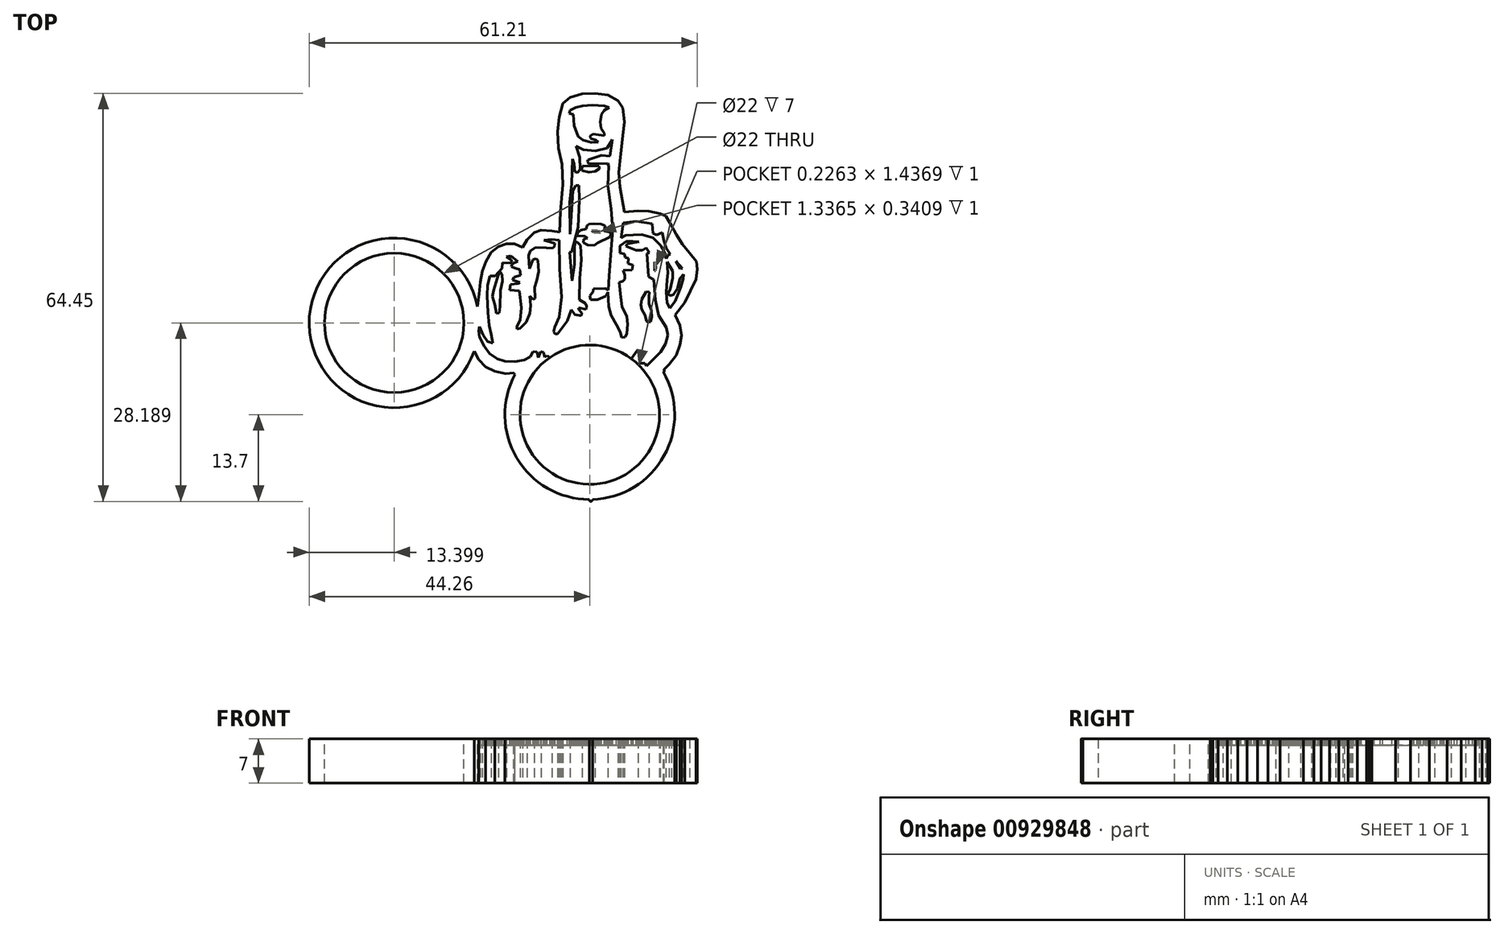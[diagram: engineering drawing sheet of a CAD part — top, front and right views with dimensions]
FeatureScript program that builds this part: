
annotation { "Feature Type Name" : "Feature", "Feature Type Description" : "" }
export const myFeature = defineFeature(function(context is Context, id is Id, definition is map)
    precondition{}
    {
        {
            var Q0;
            Q0=qCreatedBy(makeId("Top.planeOp"),FACE);
            var sketch = newSketch(context, id + "F0", { "sketchPlane" : qUnion([Q0])});
            skCircle(sketch, "E0", {"center": v(0, 0) * mm, "radius": 11 * mm});
            skCircle(sketch, "E1", {"center": v(0, 0) * mm, "radius": 13.4 * mm});
            skCircle(sketch, "E2", {"center": v(0, 0) * mm, "radius": 50.8 * mm, "construction": true});
            skLineSegment(sketch, "E3", {"start": v(0, 0) * mm, "end": v(-44, 25.4) * mm, "construction": true});
            skLineSegment(sketch, "E4", {"start": v(0, 0) * mm, "end": v(44, 25.4) * mm, "construction": true});
            skLineSegment(sketch, "E5", {"start": v(0, 0) * mm, "end": v(0, -50.8) * mm, "construction": true});
            skSolve(sketch);
        }
        {
            var Q0;
            Q0=qCreatedBy(makeId("Top.planeOp"),FACE);
            var sketch = newSketch(context, id + "F1", { "sketchPlane" : qUnion([Q0])});
            skCircle(sketch, "E6.0", {"center": v(0, 0) * mm, "radius": 13.4 * mm});
            skLineSegment(sketch, "E7", {"start": v(-11.66, 6.6) * mm, "end": v(-13.26, 6.5) * mm});
            skLineSegment(sketch, "E8", {"start": v(-13.26, 6.5) * mm, "end": v(-14.97, 6.82) * mm});
            skLineSegment(sketch, "E9", {"start": v(-14.97, 6.82) * mm, "end": v(-16.42, 7.53) * mm});
            skLineSegment(sketch, "E10", {"start": v(-16.42, 7.53) * mm, "end": v(-17.5, 8.7) * mm});
            skLineSegment(sketch, "E11", {"start": v(-17.5, 8.7) * mm, "end": v(-18.45, 10.38) * mm});
            skLineSegment(sketch, "E12", {"start": v(-18.45, 10.38) * mm, "end": v(-18.8, 12.26) * mm});
            skLineSegment(sketch, "E13", {"start": v(-18.8, 12.26) * mm, "end": v(-18.53, 13.84) * mm});
            skLineSegment(sketch, "E14", {"start": v(-18.53, 13.84) * mm, "end": v(-18.08, 14.9) * mm});
            skLineSegment(sketch, "E15", {"start": v(-18.08, 14.9) * mm, "end": v(-17.8, 16.19) * mm});
            skLineSegment(sketch, "E16", {"start": v(-17.8, 16.19) * mm, "end": v(-17.65, 17.63) * mm});
            skLineSegment(sketch, "E17", {"start": v(-17.65, 17.63) * mm, "end": v(-17.47, 19.02) * mm});
            skLineSegment(sketch, "E18", {"start": v(-17.47, 19.02) * mm, "end": v(-17.24, 20.92) * mm});
            skLineSegment(sketch, "E19", {"start": v(-17.24, 20.92) * mm, "end": v(-16.93, 22.67) * mm});
            skLineSegment(sketch, "E20", {"start": v(-16.93, 22.67) * mm, "end": v(-16.4, 24.2) * mm});
            skLineSegment(sketch, "E21", {"start": v(-16.4, 24.2) * mm, "end": v(-15.57, 25.63) * mm});
            skLineSegment(sketch, "E22", {"start": v(-15.57, 25.63) * mm, "end": v(-14.42, 26.52) * mm});
            skLineSegment(sketch, "E23", {"start": v(-14.42, 26.52) * mm, "end": v(-13.13, 26.99) * mm});
            skLineSegment(sketch, "E24", {"start": v(-13.13, 26.99) * mm, "end": v(-11.88, 26.99) * mm});
            skLineSegment(sketch, "E25", {"start": v(-11.88, 26.99) * mm, "end": v(-10.57, 26.44) * mm});
            skLineSegment(sketch, "E26", {"start": v(-10.57, 26.44) * mm, "end": v(-9.87, 27.6) * mm});
            skLineSegment(sketch, "E27", {"start": v(-9.87, 27.6) * mm, "end": v(-8.74, 28.74) * mm});
            skLineSegment(sketch, "E28", {"start": v(-8.74, 28.74) * mm, "end": v(-7.67, 29.15) * mm});
            skLineSegment(sketch, "E29", {"start": v(-7.67, 29.15) * mm, "end": v(-5.97, 29.04) * mm});
            skLineSegment(sketch, "E30", {"start": v(-5.97, 29.04) * mm, "end": v(-4.76, 28.84) * mm});
            skLineSegment(sketch, "E31", {"start": v(-4.76, 28.84) * mm, "end": v(-4.65, 32.06) * mm});
            skLineSegment(sketch, "E32", {"start": v(-4.65, 32.06) * mm, "end": v(-4.28, 36.3) * mm});
            skLineSegment(sketch, "E33", {"start": v(-4.28, 36.3) * mm, "end": v(-4.38, 39.56) * mm});
            skLineSegment(sketch, "E34", {"start": v(-4.38, 39.56) * mm, "end": v(-4.93, 42.06) * mm});
            skLineSegment(sketch, "E35", {"start": v(-4.93, 42.06) * mm, "end": v(-5.07, 44.68) * mm});
            skLineSegment(sketch, "E36", {"start": v(-5.07, 44.68) * mm, "end": v(-4.82, 46.97) * mm});
            skLineSegment(sketch, "E37", {"start": v(-4.82, 46.97) * mm, "end": v(-4.26, 49.12) * mm});
            skLineSegment(sketch, "E38", {"start": v(-4.26, 49.12) * mm, "end": v(-3.1, 50.06) * mm});
            skLineSegment(sketch, "E39", {"start": v(-3.1, 50.06) * mm, "end": v(-1.2, 50.67) * mm});
            skLineSegment(sketch, "E40", {"start": v(-1.2, 50.67) * mm, "end": v(0.84, 50.75) * mm});
            skLineSegment(sketch, "E41", {"start": v(0.84, 50.75) * mm, "end": v(2.84, 50.46) * mm});
            skLineSegment(sketch, "E42", {"start": v(2.84, 50.46) * mm, "end": v(4.45, 49.59) * mm});
            skLineSegment(sketch, "E43", {"start": v(4.45, 49.59) * mm, "end": v(5.24, 48.46) * mm});
            skLineSegment(sketch, "E44", {"start": v(5.24, 48.46) * mm, "end": v(5.47, 46.25) * mm});
            skLineSegment(sketch, "E45", {"start": v(5.47, 46.25) * mm, "end": v(5.24, 44.04) * mm});
            skLineSegment(sketch, "E46", {"start": v(5.24, 44.04) * mm, "end": v(4.88, 41.23) * mm});
            skLineSegment(sketch, "E47", {"start": v(4.88, 41.23) * mm, "end": v(4.6, 38.26) * mm});
            skLineSegment(sketch, "E48", {"start": v(4.6, 38.26) * mm, "end": v(4.78, 35.9) * mm});
            skLineSegment(sketch, "E49", {"start": v(4.78, 35.9) * mm, "end": v(5.44, 32.03) * mm});
            skLineSegment(sketch, "E50", {"start": v(5.44, 32.03) * mm, "end": v(7.63, 32.17) * mm});
            skLineSegment(sketch, "E51", {"start": v(7.63, 32.17) * mm, "end": v(9.34, 32.15) * mm});
            skLineSegment(sketch, "E52", {"start": v(9.34, 32.15) * mm, "end": v(11.1, 31.74) * mm});
            skLineSegment(sketch, "E53", {"start": v(11.1, 31.74) * mm, "end": v(12, 31.38) * mm});
            skLineSegment(sketch, "E54", {"start": v(12, 31.38) * mm, "end": v(12.92, 29.87) * mm});
            skLineSegment(sketch, "E55", {"start": v(12.92, 29.87) * mm, "end": v(13.67, 28.45) * mm});
            skLineSegment(sketch, "E56", {"start": v(13.67, 28.45) * mm, "end": v(14.6, 26.94) * mm});
            skLineSegment(sketch, "E57", {"start": v(14.6, 26.94) * mm, "end": v(15.74, 25.5) * mm});
            skLineSegment(sketch, "E58", {"start": v(15.74, 25.5) * mm, "end": v(16.8, 24.2) * mm});
            skLineSegment(sketch, "E59", {"start": v(16.8, 24.2) * mm, "end": v(16.95, 23.01) * mm});
            skLineSegment(sketch, "E60", {"start": v(16.95, 23.01) * mm, "end": v(16.77, 21.36) * mm});
            skLineSegment(sketch, "E61", {"start": v(16.77, 21.36) * mm, "end": v(14.99, 17.69) * mm});
            skLineSegment(sketch, "E62", {"start": v(14.99, 17.69) * mm, "end": v(13.47, 15.76) * mm});
            skLineSegment(sketch, "E63", {"start": v(13.47, 15.76) * mm, "end": v(14.26, 14.11) * mm});
            skLineSegment(sketch, "E64", {"start": v(14.26, 14.11) * mm, "end": v(14.47, 12.52) * mm});
            skLineSegment(sketch, "E65", {"start": v(14.47, 12.52) * mm, "end": v(14.2, 11.02) * mm});
            skLineSegment(sketch, "E66", {"start": v(14.2, 11.02) * mm, "end": v(13.68, 9.36) * mm});
            skLineSegment(sketch, "E67", {"start": v(13.68, 9.36) * mm, "end": v(12.54, 7.93) * mm});
            skLineSegment(sketch, "E68", {"start": v(12.54, 7.93) * mm, "end": v(11.5, 6.88) * mm});
            skSolve(sketch);
        }
        {
            var Q0;
            Q0=makeQuery(id+"F0.imprint","IMPRINT",FACE,{"disambiguationData":[TD([[makeQuery(id+"F0.imprint","IMPRINT",EDGE,{"derivedFrom":sQuery(id+"F0.wireOp",EDGE,"E0")}),-1.0]])]});
            extrude(context, id + "F2", {"entities" : qUnion([Q0]), "depth" : 7 * mm, "offsetDistance" : 25 * mm});
        }
        {
            var Q0;
            {var subQ0=sQuery(id+"F1.wireOp",EDGE,"E7");Q0=makeQuery(id+"F1.imprint","IMPRINT",FACE,{"disambiguationData":[TD([[makeQuery(id+"F1.imprint","IMPRINT",EDGE,{"derivedFrom":subQ0}),-1.0]])]});}
            extrude(context, id + "F3", {"entities" : qUnion([Q0]), "operationType" : NewBodyOperationType.ADD, "depth" : 7 * mm, "offsetDistance" : 25 * mm});
        }
        {
            var Q0;
            Q0=makeQuery(id+"F3.boolean.opBoolean","MERGE",FACE,{"derivedFrom":[makeQuery(id+"F2.opExtrude","CAP_FACE",FACE,{"disambiguationData":[OSD([sQuery(id+"F0.wireOp",EDGE,"E0"),sQuery(id+"F0.wireOp",EDGE,"E1")])],"isStart":false}),makeQuery(id+"F3.opExtrude","CAP_FACE",FACE,{"disambiguationData":[OSD([sQuery(id+"F1.wireOp",EDGE,"E6.0"),sQuery(id+"F1.wireOp",EDGE,"E7"),sQuery(id+"F1.wireOp",EDGE,"E8"),sQuery(id+"F1.wireOp",EDGE,"E9"),sQuery(id+"F1.wireOp",EDGE,"E10"),sQuery(id+"F1.wireOp",EDGE,"E11"),sQuery(id+"F1.wireOp",EDGE,"E12"),sQuery(id+"F1.wireOp",EDGE,"E13"),sQuery(id+"F1.wireOp",EDGE,"E14"),sQuery(id+"F1.wireOp",EDGE,"E15"),sQuery(id+"F1.wireOp",EDGE,"E16"),sQuery(id+"F1.wireOp",EDGE,"E17"),sQuery(id+"F1.wireOp",EDGE,"E18"),sQuery(id+"F1.wireOp",EDGE,"E19"),sQuery(id+"F1.wireOp",EDGE,"E20"),sQuery(id+"F1.wireOp",EDGE,"E21"),sQuery(id+"F1.wireOp",EDGE,"E22"),sQuery(id+"F1.wireOp",EDGE,"E23"),sQuery(id+"F1.wireOp",EDGE,"E24"),sQuery(id+"F1.wireOp",EDGE,"E25"),sQuery(id+"F1.wireOp",EDGE,"E26"),sQuery(id+"F1.wireOp",EDGE,"E27"),sQuery(id+"F1.wireOp",EDGE,"E28"),sQuery(id+"F1.wireOp",EDGE,"E29"),sQuery(id+"F1.wireOp",EDGE,"E30"),sQuery(id+"F1.wireOp",EDGE,"E31"),sQuery(id+"F1.wireOp",EDGE,"E32"),sQuery(id+"F1.wireOp",EDGE,"E33"),sQuery(id+"F1.wireOp",EDGE,"E34"),sQuery(id+"F1.wireOp",EDGE,"E35"),sQuery(id+"F1.wireOp",EDGE,"E36"),sQuery(id+"F1.wireOp",EDGE,"E37"),sQuery(id+"F1.wireOp",EDGE,"E38"),sQuery(id+"F1.wireOp",EDGE,"E39"),sQuery(id+"F1.wireOp",EDGE,"E40"),sQuery(id+"F1.wireOp",EDGE,"E41"),sQuery(id+"F1.wireOp",EDGE,"E42"),sQuery(id+"F1.wireOp",EDGE,"E43"),sQuery(id+"F1.wireOp",EDGE,"E44"),sQuery(id+"F1.wireOp",EDGE,"E45"),sQuery(id+"F1.wireOp",EDGE,"E46"),sQuery(id+"F1.wireOp",EDGE,"E47"),sQuery(id+"F1.wireOp",EDGE,"E48"),sQuery(id+"F1.wireOp",EDGE,"E49"),sQuery(id+"F1.wireOp",EDGE,"E50"),sQuery(id+"F1.wireOp",EDGE,"E51"),sQuery(id+"F1.wireOp",EDGE,"E52"),sQuery(id+"F1.wireOp",EDGE,"E53"),sQuery(id+"F1.wireOp",EDGE,"E54"),sQuery(id+"F1.wireOp",EDGE,"E55"),sQuery(id+"F1.wireOp",EDGE,"E56"),sQuery(id+"F1.wireOp",EDGE,"E57"),sQuery(id+"F1.wireOp",EDGE,"E58"),sQuery(id+"F1.wireOp",EDGE,"E59"),sQuery(id+"F1.wireOp",EDGE,"E60"),sQuery(id+"F1.wireOp",EDGE,"E61"),sQuery(id+"F1.wireOp",EDGE,"E62"),sQuery(id+"F1.wireOp",EDGE,"E63"),sQuery(id+"F1.wireOp",EDGE,"E64"),sQuery(id+"F1.wireOp",EDGE,"E65"),sQuery(id+"F1.wireOp",EDGE,"E66"),sQuery(id+"F1.wireOp",EDGE,"E67"),sQuery(id+"F1.wireOp",EDGE,"E68")])],"isStart":false})]});
            var sketch = newSketch(context, id + "F4", { "sketchPlane" : qUnion([Q0])});
            skLineSegment(sketch, "E69", {"start": v(-6.28, 9.03) * mm, "end": v(-6.73, 9.31) * mm});
            skLineSegment(sketch, "E70", {"start": v(-6.73, 9.31) * mm, "end": v(-7.11, 9.08) * mm});
            skLineSegment(sketch, "E71", {"start": v(-7.11, 9.08) * mm, "end": v(-7.3, 9.86) * mm});
            skLineSegment(sketch, "E72", {"start": v(-7.3, 9.86) * mm, "end": v(-7.74, 9.93) * mm});
            skLineSegment(sketch, "E73", {"start": v(-7.74, 9.93) * mm, "end": v(-8.13, 9) * mm});
            skLineSegment(sketch, "E74", {"start": v(-8.13, 9) * mm, "end": v(-8.32, 9.92) * mm});
            skLineSegment(sketch, "E75", {"start": v(-8.32, 9.92) * mm, "end": v(-8.93, 9.99) * mm});
            skLineSegment(sketch, "E76", {"start": v(-8.93, 9.99) * mm, "end": v(-9.4, 9.13) * mm});
            skLineSegment(sketch, "E77", {"start": v(-9.4, 9.13) * mm, "end": v(-10.37, 8.6) * mm});
            skLineSegment(sketch, "E78", {"start": v(-10.37, 8.6) * mm, "end": v(-11.8, 8.35) * mm});
            skLineSegment(sketch, "E79", {"start": v(-11.8, 8.35) * mm, "end": v(-13.42, 8.46) * mm});
            skLineSegment(sketch, "E80", {"start": v(-13.42, 8.46) * mm, "end": v(-14.6, 8.84) * mm});
            skLineSegment(sketch, "E81", {"start": v(-14.6, 8.84) * mm, "end": v(-15.77, 9.67) * mm});
            skLineSegment(sketch, "E82", {"start": v(-15.77, 9.67) * mm, "end": v(-16.6, 10.77) * mm});
            skLineSegment(sketch, "E83", {"start": v(-16.6, 10.77) * mm, "end": v(-17.36, 12.26) * mm});
            skLineSegment(sketch, "E84", {"start": v(-17.36, 12.26) * mm, "end": v(-17.52, 13.2) * mm});
            skLineSegment(sketch, "E85", {"start": v(-17.52, 13.2) * mm, "end": v(-17.37, 13.87) * mm});
            skLineSegment(sketch, "E86", {"start": v(-17.37, 13.87) * mm, "end": v(-16.84, 12.58) * mm});
            skLineSegment(sketch, "E87", {"start": v(-16.84, 12.58) * mm, "end": v(-16.14, 11.55) * mm});
            skLineSegment(sketch, "E88", {"start": v(-16.14, 11.55) * mm, "end": v(-15.3, 11.3) * mm});
            skLineSegment(sketch, "E89", {"start": v(-15.3, 11.3) * mm, "end": v(-15.55, 12.68) * mm});
            skLineSegment(sketch, "E90", {"start": v(-15.55, 12.68) * mm, "end": v(-15.87, 14.1) * mm});
            skLineSegment(sketch, "E91", {"start": v(-15.87, 14.1) * mm, "end": v(-16.07, 16.12) * mm});
            skLineSegment(sketch, "E92", {"start": v(-16.07, 16.12) * mm, "end": v(-16.2, 18.8) * mm});
            skLineSegment(sketch, "E93", {"start": v(-16.2, 18.8) * mm, "end": v(-16.1, 20.45) * mm});
            skLineSegment(sketch, "E94", {"start": v(-16.1, 20.45) * mm, "end": v(-15.74, 21.88) * mm});
            skLineSegment(sketch, "E95", {"start": v(-15.74, 21.88) * mm, "end": v(-14.91, 21.88) * mm});
            skLineSegment(sketch, "E96", {"start": v(-14.91, 21.88) * mm, "end": v(-13.81, 23.14) * mm});
            skLineSegment(sketch, "E97", {"start": v(-13.81, 23.14) * mm, "end": v(-13.8, 24.01) * mm});
            skLineSegment(sketch, "E98", {"start": v(-13.8, 24.01) * mm, "end": v(-12.59, 23.92) * mm});
            skLineSegment(sketch, "E99", {"start": v(-12.59, 23.92) * mm, "end": v(-12.22, 24.1) * mm});
            skLineSegment(sketch, "E100", {"start": v(-12.22, 24.1) * mm, "end": v(-12.41, 24.52) * mm});
            skLineSegment(sketch, "E101", {"start": v(-12.41, 24.52) * mm, "end": v(-13.13, 24.93) * mm});
            skLineSegment(sketch, "E102", {"start": v(-13.13, 24.93) * mm, "end": v(-12.47, 25.06) * mm});
            skLineSegment(sketch, "E103", {"start": v(-12.47, 25.06) * mm, "end": v(-11.38, 24.18) * mm});
            skLineSegment(sketch, "E104", {"start": v(-11.38, 24.18) * mm, "end": v(-12.17, 23.84) * mm});
            skLineSegment(sketch, "E105", {"start": v(-12.17, 23.84) * mm, "end": v(-12.37, 23.34) * mm});
            skLineSegment(sketch, "E106", {"start": v(-12.37, 23.34) * mm, "end": v(-11.69, 23.1) * mm});
            skLineSegment(sketch, "E107", {"start": v(-11.69, 23.1) * mm, "end": v(-11.03, 22.92) * mm});
            skLineSegment(sketch, "E108", {"start": v(-11.03, 22.92) * mm, "end": v(-10.93, 22.05) * mm});
            skLineSegment(sketch, "E109", {"start": v(-10.93, 22.05) * mm, "end": v(-11.92, 21.73) * mm});
            skLineSegment(sketch, "E110", {"start": v(-11.92, 21.73) * mm, "end": v(-12.18, 21.27) * mm});
            skLineSegment(sketch, "E111", {"start": v(-12.18, 21.27) * mm, "end": v(-11.03, 20.88) * mm});
            skLineSegment(sketch, "E112", {"start": v(-11.03, 20.88) * mm, "end": v(-11.37, 20.72) * mm});
            skLineSegment(sketch, "E113", {"start": v(-11.37, 20.72) * mm, "end": v(-12.51, 20.53) * mm});
            skLineSegment(sketch, "E114", {"start": v(-12.51, 20.53) * mm, "end": v(-12.66, 19.7) * mm});
            skLineSegment(sketch, "E115", {"start": v(-12.66, 19.7) * mm, "end": v(-11.12, 19.54) * mm});
            skLineSegment(sketch, "E116", {"start": v(-11.12, 19.54) * mm, "end": v(-10.78, 16.9) * mm});
            skLineSegment(sketch, "E117", {"start": v(-10.78, 16.9) * mm, "end": v(-10.96, 14.9) * mm});
            skLineSegment(sketch, "E118", {"start": v(-10.96, 14.9) * mm, "end": v(-11.48, 13.96) * mm});
            skLineSegment(sketch, "E119", {"start": v(-11.48, 13.96) * mm, "end": v(-11.47, 13.55) * mm});
            skLineSegment(sketch, "E120", {"start": v(-11.47, 13.55) * mm, "end": v(-10.97, 13.62) * mm});
            skLineSegment(sketch, "E121", {"start": v(-10.97, 13.62) * mm, "end": v(-10, 14.57) * mm});
            skLineSegment(sketch, "E122", {"start": v(-10, 14.57) * mm, "end": v(-9.44, 16.02) * mm});
            skLineSegment(sketch, "E123", {"start": v(-9.44, 16.02) * mm, "end": v(-9.3, 17.2) * mm});
            skLineSegment(sketch, "E124", {"start": v(-9.3, 17.2) * mm, "end": v(-9.46, 18.7) * mm});
            skLineSegment(sketch, "E125", {"start": v(-9.46, 18.7) * mm, "end": v(-8.96, 18.2) * mm});
            skLineSegment(sketch, "E126", {"start": v(-8.96, 18.2) * mm, "end": v(-8.66, 18.35) * mm});
            skLineSegment(sketch, "E127", {"start": v(-8.66, 18.35) * mm, "end": v(-8.68, 20.14) * mm});
            skLineSegment(sketch, "E128", {"start": v(-8.68, 20.14) * mm, "end": v(-8.36, 21.12) * mm});
            skLineSegment(sketch, "E129", {"start": v(-8.36, 21.12) * mm, "end": v(-8.04, 22.57) * mm});
            skLineSegment(sketch, "E130", {"start": v(-8.04, 22.57) * mm, "end": v(-8.17, 24.4) * mm});
            skLineSegment(sketch, "E131", {"start": v(-8.17, 24.4) * mm, "end": v(-8.47, 24.62) * mm});
            skLineSegment(sketch, "E132", {"start": v(-8.47, 24.62) * mm, "end": v(-8.93, 24.51) * mm});
            skLineSegment(sketch, "E133", {"start": v(-8.93, 24.51) * mm, "end": v(-9.55, 23.02) * mm});
            skLineSegment(sketch, "E134", {"start": v(-9.55, 23.02) * mm, "end": v(-9.62, 25.13) * mm});
            skLineSegment(sketch, "E135", {"start": v(-9.62, 25.13) * mm, "end": v(-9.36, 25.81) * mm});
            skLineSegment(sketch, "E136", {"start": v(-9.36, 25.81) * mm, "end": v(-8.56, 26.4) * mm});
            skLineSegment(sketch, "E137", {"start": v(-8.56, 26.4) * mm, "end": v(-6.87, 26.32) * mm});
            skLineSegment(sketch, "E138", {"start": v(-6.87, 26.32) * mm, "end": v(-5.9, 26.28) * mm});
            skLineSegment(sketch, "E139", {"start": v(-5.9, 26.28) * mm, "end": v(-5.56, 26.56) * mm});
            skLineSegment(sketch, "E140", {"start": v(-5.56, 26.56) * mm, "end": v(-5.52, 27.04) * mm});
            skLineSegment(sketch, "E141", {"start": v(-5.52, 27.04) * mm, "end": v(-7.22, 27.53) * mm});
            skLineSegment(sketch, "E142", {"start": v(-7.22, 27.53) * mm, "end": v(-6, 27.66) * mm});
            skLineSegment(sketch, "E143", {"start": v(-6, 27.66) * mm, "end": v(-4.84, 27.55) * mm});
            skLineSegment(sketch, "E144", {"start": v(-4.84, 27.55) * mm, "end": v(-4.73, 23) * mm});
            skLineSegment(sketch, "E145", {"start": v(-4.73, 23) * mm, "end": v(-4.43, 18.61) * mm});
            skLineSegment(sketch, "E146", {"start": v(-4.43, 18.61) * mm, "end": v(-4.83, 15.4) * mm});
            skLineSegment(sketch, "E147", {"start": v(-4.83, 15.4) * mm, "end": v(-5.53, 13.85) * mm});
            skLineSegment(sketch, "E148", {"start": v(-5.53, 13.85) * mm, "end": v(-5.7, 13.08) * mm});
            skLineSegment(sketch, "E149", {"start": v(-5.7, 13.08) * mm, "end": v(-5.44, 12.76) * mm});
            skLineSegment(sketch, "E150", {"start": v(-5.44, 12.76) * mm, "end": v(-5.09, 12.77) * mm});
            skLineSegment(sketch, "E151", {"start": v(-5.09, 12.77) * mm, "end": v(-3.56, 14.79) * mm});
            skLineSegment(sketch, "E152", {"start": v(-3.56, 14.79) * mm, "end": v(-2.94, 16.55) * mm});
            skLineSegment(sketch, "E153", {"start": v(-2.94, 16.55) * mm, "end": v(-2.35, 15.78) * mm});
            skLineSegment(sketch, "E154", {"start": v(-2.35, 15.78) * mm, "end": v(-1.34, 15.59) * mm});
            skLineSegment(sketch, "E155", {"start": v(-1.34, 15.59) * mm, "end": v(-1.24, 16.08) * mm});
            skLineSegment(sketch, "E156", {"start": v(-1.24, 16.08) * mm, "end": v(-1.7, 16.55) * mm});
            skLineSegment(sketch, "E157", {"start": v(-1.7, 16.55) * mm, "end": v(-1.78, 16.88) * mm});
            skLineSegment(sketch, "E158", {"start": v(-1.78, 16.88) * mm, "end": v(-0.6, 16.65) * mm});
            skLineSegment(sketch, "E159", {"start": v(-0.6, 16.65) * mm, "end": v(-0.48, 17.12) * mm});
            skLineSegment(sketch, "E160", {"start": v(-0.48, 17.12) * mm, "end": v(-0.72, 17.56) * mm});
            skLineSegment(sketch, "E161", {"start": v(-0.72, 17.56) * mm, "end": v(-1.65, 18.16) * mm});
            skLineSegment(sketch, "E162", {"start": v(-1.65, 18.16) * mm, "end": v(-1.58, 21.5) * mm});
            skLineSegment(sketch, "E163", {"start": v(-1.58, 21.5) * mm, "end": v(-1.33, 24.47) * mm});
            skLineSegment(sketch, "E164", {"start": v(-1.33, 24.47) * mm, "end": v(-1.46, 26.71) * mm});
            skLineSegment(sketch, "E165", {"start": v(-1.46, 26.71) * mm, "end": v(-1.97, 27.24) * mm});
            skLineSegment(sketch, "E166", {"start": v(-1.97, 27.24) * mm, "end": v(-2.31, 27.21) * mm});
            skLineSegment(sketch, "E167", {"start": v(-2.31, 27.21) * mm, "end": v(-2.43, 26.57) * mm});
            skLineSegment(sketch, "E168", {"start": v(-2.43, 26.57) * mm, "end": v(-2.44, 23.76) * mm});
            skLineSegment(sketch, "E169", {"start": v(-2.44, 23.76) * mm, "end": v(-2.81, 21.13) * mm});
            skLineSegment(sketch, "E170", {"start": v(-2.81, 21.13) * mm, "end": v(-3.18, 25.64) * mm});
            skLineSegment(sketch, "E171", {"start": v(-3.18, 25.64) * mm, "end": v(-2.84, 25.7) * mm});
            skLineSegment(sketch, "E172", {"start": v(-2.84, 25.7) * mm, "end": v(-1.83, 29.61) * mm});
            skLineSegment(sketch, "E173", {"start": v(-1.83, 29.61) * mm, "end": v(-1.62, 33.92) * mm});
            skLineSegment(sketch, "E174", {"start": v(-1.62, 33.92) * mm, "end": v(-1.73, 36.16) * mm});
            skLineSegment(sketch, "E175", {"start": v(-1.73, 36.16) * mm, "end": v(-2.24, 36.2) * mm});
            skLineSegment(sketch, "E176", {"start": v(-2.24, 36.2) * mm, "end": v(-2.64, 35.35) * mm});
            skLineSegment(sketch, "E177", {"start": v(-2.64, 35.35) * mm, "end": v(-3.08, 28.52) * mm});
            skLineSegment(sketch, "E178", {"start": v(-3.08, 28.52) * mm, "end": v(-3.15, 33.53) * mm});
            skLineSegment(sketch, "E179", {"start": v(-3.15, 33.53) * mm, "end": v(-2.86, 36.43) * mm});
            skLineSegment(sketch, "E180", {"start": v(-2.86, 36.43) * mm, "end": v(-2.75, 40.4) * mm});
            skLineSegment(sketch, "E181", {"start": v(-2.75, 40.4) * mm, "end": v(-2.47, 39.64) * mm});
            skLineSegment(sketch, "E182", {"start": v(-2.47, 39.64) * mm, "end": v(-2.37, 38.33) * mm});
            skLineSegment(sketch, "E183", {"start": v(-2.37, 38.33) * mm, "end": v(-1.9, 38.19) * mm});
            skLineSegment(sketch, "E184", {"start": v(-1.9, 38.19) * mm, "end": v(-1.53, 38.77) * mm});
            skLineSegment(sketch, "E185", {"start": v(-1.53, 38.77) * mm, "end": v(-1.58, 40.62) * mm});
            skLineSegment(sketch, "E186", {"start": v(-1.58, 40.62) * mm, "end": v(-2.14, 42.43) * mm});
            skLineSegment(sketch, "E187", {"start": v(-2.14, 42.43) * mm, "end": v(-0.98, 41.84) * mm});
            skLineSegment(sketch, "E188", {"start": v(-0.98, 41.84) * mm, "end": v(0.88, 41.62) * mm});
            skLineSegment(sketch, "E189", {"start": v(0.88, 41.62) * mm, "end": v(2.72, 42.1) * mm});
            skLineSegment(sketch, "E190", {"start": v(2.72, 42.1) * mm, "end": v(3.53, 43.4) * mm});
            skLineSegment(sketch, "E191", {"start": v(3.53, 43.4) * mm, "end": v(3.2, 40.8) * mm});
            skLineSegment(sketch, "E192", {"start": v(3.2, 40.8) * mm, "end": v(1.83, 40.95) * mm});
            skLineSegment(sketch, "E193", {"start": v(1.83, 40.95) * mm, "end": v(-0.27, 40.28) * mm});
            skLineSegment(sketch, "E194", {"start": v(-0.27, 40.28) * mm, "end": v(-0.36, 39.92) * mm});
            skLineSegment(sketch, "E195", {"start": v(-0.36, 39.92) * mm, "end": v(-0.14, 39.59) * mm});
            skLineSegment(sketch, "E196", {"start": v(-0.14, 39.59) * mm, "end": v(2.77, 39.65) * mm});
            skLineSegment(sketch, "E197", {"start": v(2.77, 39.65) * mm, "end": v(2.99, 39.34) * mm});
            skLineSegment(sketch, "E198", {"start": v(2.99, 39.34) * mm, "end": v(2.86, 36.15) * mm});
            skLineSegment(sketch, "E199", {"start": v(2.86, 36.15) * mm, "end": v(3.4, 32.53) * mm});
            skLineSegment(sketch, "E200", {"start": v(3.4, 32.53) * mm, "end": v(3.63, 29.2) * mm});
            skLineSegment(sketch, "E201", {"start": v(3.63, 29.2) * mm, "end": v(3.43, 26.86) * mm});
            skLineSegment(sketch, "E202", {"start": v(3.43, 26.86) * mm, "end": v(3.02, 21.89) * mm});
            skLineSegment(sketch, "E203", {"start": v(3.02, 21.89) * mm, "end": v(2.9, 19.7) * mm});
            skLineSegment(sketch, "E204", {"start": v(2.9, 19.7) * mm, "end": v(2.4, 19.93) * mm});
            skLineSegment(sketch, "E205", {"start": v(2.4, 19.93) * mm, "end": v(0.59, 19.9) * mm});
            skLineSegment(sketch, "E206", {"start": v(0.59, 19.9) * mm, "end": v(0.48, 19.34) * mm});
            skLineSegment(sketch, "E207", {"start": v(0.48, 19.34) * mm, "end": v(0.02, 18.76) * mm});
            skLineSegment(sketch, "E208", {"start": v(0.02, 18.76) * mm, "end": v(0.15, 18.13) * mm});
            skLineSegment(sketch, "E209", {"start": v(0.15, 18.13) * mm, "end": v(1.23, 18.18) * mm});
            skLineSegment(sketch, "E210", {"start": v(1.23, 18.18) * mm, "end": v(2.55, 18.74) * mm});
            skLineSegment(sketch, "E211", {"start": v(2.55, 18.74) * mm, "end": v(2.88, 19.38) * mm});
            skLineSegment(sketch, "E212", {"start": v(2.88, 19.38) * mm, "end": v(3, 17.1) * mm});
            skLineSegment(sketch, "E213", {"start": v(3, 17.1) * mm, "end": v(3.35, 15.7) * mm});
            skLineSegment(sketch, "E214", {"start": v(3.35, 15.7) * mm, "end": v(4.21, 14.2) * mm});
            skLineSegment(sketch, "E215", {"start": v(4.21, 14.2) * mm, "end": v(4.84, 13.03) * mm});
            skLineSegment(sketch, "E216", {"start": v(4.84, 13.03) * mm, "end": v(5, 12.2) * mm});
            skLineSegment(sketch, "E217", {"start": v(5, 12.2) * mm, "end": v(5.58, 12.25) * mm});
            skLineSegment(sketch, "E218", {"start": v(5.58, 12.25) * mm, "end": v(5.86, 12.8) * mm});
            skLineSegment(sketch, "E219", {"start": v(5.86, 12.8) * mm, "end": v(6, 14.3) * mm});
            skLineSegment(sketch, "E220", {"start": v(6, 14.3) * mm, "end": v(5.85, 15.48) * mm});
            skLineSegment(sketch, "E221", {"start": v(5.85, 15.48) * mm, "end": v(5.09, 17.06) * mm});
            skLineSegment(sketch, "E222", {"start": v(5.09, 17.06) * mm, "end": v(4.92, 18.5) * mm});
            skLineSegment(sketch, "E223", {"start": v(4.92, 18.5) * mm, "end": v(4.63, 20.88) * mm});
            skLineSegment(sketch, "E224", {"start": v(4.63, 20.88) * mm, "end": v(5.2, 21.1) * mm});
            skLineSegment(sketch, "E225", {"start": v(5.2, 21.1) * mm, "end": v(5.53, 21.39) * mm});
            skLineSegment(sketch, "E226", {"start": v(5.53, 21.39) * mm, "end": v(5.55, 22.03) * mm});
            skLineSegment(sketch, "E227", {"start": v(5.55, 22.03) * mm, "end": v(5.28, 22.77) * mm});
            skLineSegment(sketch, "E228", {"start": v(5.28, 22.77) * mm, "end": v(6.7, 22.86) * mm});
            skLineSegment(sketch, "E229", {"start": v(6.7, 22.86) * mm, "end": v(6.8, 23.64) * mm});
            skLineSegment(sketch, "E230", {"start": v(6.8, 23.64) * mm, "end": v(6.05, 23.85) * mm});
            skLineSegment(sketch, "E231", {"start": v(6.05, 23.85) * mm, "end": v(6.08, 24.66) * mm});
            skLineSegment(sketch, "E232", {"start": v(6.08, 24.66) * mm, "end": v(5.58, 24.83) * mm});
            skLineSegment(sketch, "E233", {"start": v(5.58, 24.83) * mm, "end": v(5.47, 25.37) * mm});
            skLineSegment(sketch, "E234", {"start": v(5.47, 25.37) * mm, "end": v(4.78, 25.5) * mm});
            skLineSegment(sketch, "E235", {"start": v(4.78, 25.5) * mm, "end": v(4.8, 26.65) * mm});
            skLineSegment(sketch, "E236", {"start": v(4.8, 26.65) * mm, "end": v(5.84, 27.41) * mm});
            skLineSegment(sketch, "E237", {"start": v(5.84, 27.41) * mm, "end": v(7.73, 27.3) * mm});
            skLineSegment(sketch, "E238", {"start": v(7.73, 27.3) * mm, "end": v(5.89, 27) * mm});
            skLineSegment(sketch, "E239", {"start": v(5.89, 27) * mm, "end": v(5.7, 26.63) * mm});
            skLineSegment(sketch, "E240", {"start": v(5.7, 26.63) * mm, "end": v(7.3, 25.97) * mm});
            skLineSegment(sketch, "E241", {"start": v(7.3, 25.97) * mm, "end": v(8.34, 25.94) * mm});
            skLineSegment(sketch, "E242", {"start": v(8.34, 25.94) * mm, "end": v(8.9, 26.33) * mm});
            skLineSegment(sketch, "E243", {"start": v(8.9, 26.33) * mm, "end": v(9.42, 25.6) * mm});
            skLineSegment(sketch, "E244", {"start": v(9.42, 25.6) * mm, "end": v(9.05, 25.48) * mm});
            skLineSegment(sketch, "E245", {"start": v(9.05, 25.48) * mm, "end": v(9.3, 21.78) * mm});
            skLineSegment(sketch, "E246", {"start": v(9.3, 21.78) * mm, "end": v(10.11, 21.36) * mm});
            skLineSegment(sketch, "E247", {"start": v(10.11, 21.36) * mm, "end": v(10.36, 18.08) * mm});
            skLineSegment(sketch, "E248", {"start": v(10.36, 18.08) * mm, "end": v(10.84, 15.68) * mm});
            skLineSegment(sketch, "E249", {"start": v(10.84, 15.68) * mm, "end": v(12.05, 13.77) * mm});
            skLineSegment(sketch, "E250", {"start": v(12.05, 13.77) * mm, "end": v(12.32, 12.56) * mm});
            skLineSegment(sketch, "E251", {"start": v(12.32, 12.56) * mm, "end": v(11.96, 11.15) * mm});
            skLineSegment(sketch, "E252", {"start": v(11.96, 11.15) * mm, "end": v(11.18, 9.9) * mm});
            skLineSegment(sketch, "E253", {"start": v(11.18, 9.9) * mm, "end": v(8.95, 7.7) * mm});
            skLineSegment(sketch, "E254", {"start": v(8.95, 7.7) * mm, "end": v(8.73, 8.1) * mm});
            skLineSegment(sketch, "E255", {"start": v(8.73, 8.1) * mm, "end": v(7.96, 8.13) * mm});
            skLineSegment(sketch, "E256", {"start": v(7.96, 8.13) * mm, "end": v(8.1, 10.06) * mm});
            skLineSegment(sketch, "E257", {"start": v(8.1, 10.06) * mm, "end": v(7.49, 10.15) * mm});
            skLineSegment(sketch, "E258", {"start": v(7.49, 10.15) * mm, "end": v(6.52, 8.8) * mm});
            skLineSegment(sketch, "E259", {"start": v(-3.24, 47.52) * mm, "end": v(-2.6, 47.44) * mm});
            skLineSegment(sketch, "E260", {"start": v(-2.6, 47.44) * mm, "end": v(-2.46, 45.64) * mm});
            skLineSegment(sketch, "E261", {"start": v(-2.46, 45.64) * mm, "end": v(-1.86, 43.96) * mm});
            skLineSegment(sketch, "E262", {"start": v(-1.86, 43.96) * mm, "end": v(-1.08, 43.34) * mm});
            skLineSegment(sketch, "E263", {"start": v(-1.08, 43.34) * mm, "end": v(0.29, 43) * mm});
            skLineSegment(sketch, "E264", {"start": v(0.29, 43) * mm, "end": v(1.32, 43.07) * mm});
            skLineSegment(sketch, "E265", {"start": v(1.32, 43.07) * mm, "end": v(0.97, 43.38) * mm});
            skLineSegment(sketch, "E266", {"start": v(0.97, 43.38) * mm, "end": v(0.14, 43.6) * mm});
            skLineSegment(sketch, "E267", {"start": v(0.14, 43.6) * mm, "end": v(0.08, 44.02) * mm});
            skLineSegment(sketch, "E268", {"start": v(0.08, 44.02) * mm, "end": v(0.5, 44.34) * mm});
            skLineSegment(sketch, "E269", {"start": v(0.5, 44.34) * mm, "end": v(2.29, 44.07) * mm});
            skLineSegment(sketch, "E270", {"start": v(2.29, 44.07) * mm, "end": v(2.29, 44.42) * mm});
            skLineSegment(sketch, "E271", {"start": v(2.29, 44.42) * mm, "end": v(1.76, 45.2) * mm});
            skLineSegment(sketch, "E272", {"start": v(1.76, 45.2) * mm, "end": v(1.63, 46.25) * mm});
            skLineSegment(sketch, "E273", {"start": v(1.63, 46.25) * mm, "end": v(1.87, 47.45) * mm});
            skLineSegment(sketch, "E274", {"start": v(1.87, 47.45) * mm, "end": v(2.27, 48.08) * mm});
            skLineSegment(sketch, "E275", {"start": v(2.27, 48.08) * mm, "end": v(3.07, 48.49) * mm});
            skLineSegment(sketch, "E276", {"start": v(3.07, 48.49) * mm, "end": v(2.3, 48.75) * mm});
            skLineSegment(sketch, "E277", {"start": v(2.3, 48.75) * mm, "end": v(0.39, 48.9) * mm});
            skLineSegment(sketch, "E278", {"start": v(0.39, 48.9) * mm, "end": v(-1.13, 48.78) * mm});
            skLineSegment(sketch, "E279", {"start": v(-1.13, 48.78) * mm, "end": v(-2.24, 48.53) * mm});
            skLineSegment(sketch, "E280", {"start": v(-2.24, 48.53) * mm, "end": v(-3.09, 48.03) * mm});
            skLineSegment(sketch, "E281", {"start": v(-3.09, 48.03) * mm, "end": v(-3.24, 47.52) * mm});
            skLineSegment(sketch, "E282", {"start": v(-1.14, 39.29) * mm, "end": v(-1.3, 38.77) * mm});
            skLineSegment(sketch, "E283", {"start": v(-1.3, 38.77) * mm, "end": v(-1.18, 38.55) * mm});
            skLineSegment(sketch, "E284", {"start": v(-1.18, 38.55) * mm, "end": v(-0.14, 38.28) * mm});
            skLineSegment(sketch, "E285", {"start": v(-0.14, 38.28) * mm, "end": v(0.8, 38.4) * mm});
            skLineSegment(sketch, "E286", {"start": v(0.8, 38.4) * mm, "end": v(1.51, 38.86) * mm});
            skLineSegment(sketch, "E287", {"start": v(1.51, 38.86) * mm, "end": v(1.48, 39.26) * mm});
            skLineSegment(sketch, "E288", {"start": v(1.48, 39.26) * mm, "end": v(-1.14, 39.29) * mm});
            skLineSegment(sketch, "E289", {"start": v(0.3, 29.1) * mm, "end": v(0.62, 28.8) * mm});
            skLineSegment(sketch, "E290", {"start": v(0.62, 28.8) * mm, "end": v(1.63, 28.75) * mm});
            skLineSegment(sketch, "E291", {"start": v(1.63, 28.75) * mm, "end": v(1.16, 29.04) * mm});
            skLineSegment(sketch, "E292", {"start": v(1.16, 29.04) * mm, "end": v(0.3, 29.1) * mm});
            skLineSegment(sketch, "E293", {"start": v(-0.56, 29.33) * mm, "end": v(-1.4, 29.12) * mm});
            skLineSegment(sketch, "E294", {"start": v(-1.4, 29.12) * mm, "end": v(-1.93, 28.74) * mm});
            skLineSegment(sketch, "E295", {"start": v(-1.93, 28.74) * mm, "end": v(-1.98, 28.23) * mm});
            skLineSegment(sketch, "E296", {"start": v(-1.98, 28.23) * mm, "end": v(-0.76, 28.22) * mm});
            skLineSegment(sketch, "E297", {"start": v(-0.76, 28.22) * mm, "end": v(-0.36, 27.9) * mm});
            skLineSegment(sketch, "E298", {"start": v(-0.36, 27.9) * mm, "end": v(-0.92, 27.77) * mm});
            skLineSegment(sketch, "E299", {"start": v(-0.92, 27.77) * mm, "end": v(-0.99, 27.15) * mm});
            skLineSegment(sketch, "E300", {"start": v(-0.99, 27.15) * mm, "end": v(-0.3, 26.8) * mm});
            skLineSegment(sketch, "E301", {"start": v(-0.3, 26.8) * mm, "end": v(0.71, 26.75) * mm});
            skLineSegment(sketch, "E302", {"start": v(0.71, 26.75) * mm, "end": v(1.23, 27.1) * mm});
            skLineSegment(sketch, "E303", {"start": v(1.23, 27.1) * mm, "end": v(3.15, 28.08) * mm});
            skLineSegment(sketch, "E304", {"start": v(3.15, 28.08) * mm, "end": v(3.4, 28.53) * mm});
            skLineSegment(sketch, "E305", {"start": v(3.4, 28.53) * mm, "end": v(3.14, 28.82) * mm});
            skLineSegment(sketch, "E306", {"start": v(3.14, 28.82) * mm, "end": v(2.3, 28.98) * mm});
            skLineSegment(sketch, "E307", {"start": v(2.3, 28.98) * mm, "end": v(2.4, 29.8) * mm});
            skLineSegment(sketch, "E308", {"start": v(2.4, 29.8) * mm, "end": v(1.8, 30.06) * mm});
            skLineSegment(sketch, "E309", {"start": v(1.8, 30.06) * mm, "end": v(0.64, 30.16) * mm});
            skLineSegment(sketch, "E310", {"start": v(0.64, 30.16) * mm, "end": v(-0.15, 30.07) * mm});
            skLineSegment(sketch, "E311", {"start": v(-0.15, 30.07) * mm, "end": v(-0.47, 29.82) * mm});
            skLineSegment(sketch, "E312", {"start": v(-0.47, 29.82) * mm, "end": v(-0.56, 29.33) * mm});
            skLineSegment(sketch, "E313", {"start": v(-14.73, 16.01) * mm, "end": v(-14.27, 16.03) * mm});
            skLineSegment(sketch, "E314", {"start": v(-14.27, 16.03) * mm, "end": v(-14.16, 17.05) * mm});
            skLineSegment(sketch, "E315", {"start": v(-14.16, 17.05) * mm, "end": v(-14.09, 19.59) * mm});
            skLineSegment(sketch, "E316", {"start": v(-14.09, 19.59) * mm, "end": v(-13.79, 21.1) * mm});
            skLineSegment(sketch, "E317", {"start": v(-13.79, 21.1) * mm, "end": v(-13.82, 22.13) * mm});
            skLineSegment(sketch, "E318", {"start": v(-13.82, 22.13) * mm, "end": v(-14.1, 22.46) * mm});
            skLineSegment(sketch, "E319", {"start": v(-14.1, 22.46) * mm, "end": v(-14.3, 22.42) * mm});
            skLineSegment(sketch, "E320", {"start": v(-14.3, 22.42) * mm, "end": v(-14.59, 21.52) * mm});
            skLineSegment(sketch, "E321", {"start": v(-14.59, 21.52) * mm, "end": v(-15.2, 19.62) * mm});
            skLineSegment(sketch, "E322", {"start": v(-15.2, 19.62) * mm, "end": v(-15.34, 18.67) * mm});
            skLineSegment(sketch, "E323", {"start": v(-15.34, 18.67) * mm, "end": v(-14.99, 17.4) * mm});
            skLineSegment(sketch, "E324", {"start": v(-14.99, 17.4) * mm, "end": v(-14.73, 16.01) * mm});
            skLineSegment(sketch, "E325", {"start": v(8.93, 14.8) * mm, "end": v(8.72, 15.73) * mm});
            skLineSegment(sketch, "E326", {"start": v(8.72, 15.73) * mm, "end": v(8.19, 16.65) * mm});
            skLineSegment(sketch, "E327", {"start": v(8.19, 16.65) * mm, "end": v(8.08, 17.3) * mm});
            skLineSegment(sketch, "E328", {"start": v(8.08, 17.3) * mm, "end": v(8.22, 18.2) * mm});
            skLineSegment(sketch, "E329", {"start": v(8.22, 18.2) * mm, "end": v(8.87, 19.4) * mm});
            skLineSegment(sketch, "E330", {"start": v(8.87, 19.4) * mm, "end": v(9.43, 19.4) * mm});
            skLineSegment(sketch, "E331", {"start": v(9.43, 19.4) * mm, "end": v(9.34, 18.68) * mm});
            skLineSegment(sketch, "E332", {"start": v(9.34, 18.68) * mm, "end": v(9.34, 17.54) * mm});
            skLineSegment(sketch, "E333", {"start": v(9.34, 17.54) * mm, "end": v(9.69, 16.46) * mm});
            skLineSegment(sketch, "E334", {"start": v(9.69, 16.46) * mm, "end": v(9.77, 15.44) * mm});
            skLineSegment(sketch, "E335", {"start": v(9.77, 15.44) * mm, "end": v(9.6, 14.67) * mm});
            skLineSegment(sketch, "E336", {"start": v(9.6, 14.67) * mm, "end": v(9.17, 14.62) * mm});
            skLineSegment(sketch, "E337", {"start": v(9.17, 14.62) * mm, "end": v(8.93, 14.8) * mm});
            skLineSegment(sketch, "E338", {"start": v(4.95, 27.96) * mm, "end": v(5.28, 30.3) * mm});
            skLineSegment(sketch, "E339", {"start": v(5.28, 30.3) * mm, "end": v(7.29, 30.55) * mm});
            skLineSegment(sketch, "E340", {"start": v(7.29, 30.55) * mm, "end": v(9.85, 30.16) * mm});
            skLineSegment(sketch, "E341", {"start": v(9.85, 30.16) * mm, "end": v(9.97, 28.6) * mm});
            skLineSegment(sketch, "E342", {"start": v(9.97, 28.6) * mm, "end": v(10.52, 28.4) * mm});
            skLineSegment(sketch, "E343", {"start": v(10.52, 28.4) * mm, "end": v(11.43, 28.74) * mm});
            skLineSegment(sketch, "E344", {"start": v(11.43, 28.74) * mm, "end": v(11.7, 27.48) * mm});
            skLineSegment(sketch, "E345", {"start": v(11.7, 27.48) * mm, "end": v(12.1, 26.27) * mm});
            skLineSegment(sketch, "E346", {"start": v(12.1, 26.27) * mm, "end": v(12.69, 25.3) * mm});
            skLineSegment(sketch, "E347", {"start": v(12.69, 25.3) * mm, "end": v(12.31, 25.2) * mm});
            skLineSegment(sketch, "E348", {"start": v(12.31, 25.2) * mm, "end": v(12.08, 24.63) * mm});
            skLineSegment(sketch, "E349", {"start": v(12.08, 24.63) * mm, "end": v(11.83, 25.58) * mm});
            skLineSegment(sketch, "E350", {"start": v(11.83, 25.58) * mm, "end": v(11.16, 26.73) * mm});
            skLineSegment(sketch, "E351", {"start": v(11.16, 26.73) * mm, "end": v(9.95, 27.9) * mm});
            skLineSegment(sketch, "E352", {"start": v(9.95, 27.9) * mm, "end": v(8.19, 28.44) * mm});
            skLineSegment(sketch, "E353", {"start": v(8.19, 28.44) * mm, "end": v(6.88, 28.4) * mm});
            skLineSegment(sketch, "E354", {"start": v(6.88, 28.4) * mm, "end": v(5.67, 28.29) * mm});
            skLineSegment(sketch, "E355", {"start": v(5.67, 28.29) * mm, "end": v(4.95, 27.96) * mm});
            skLineSegment(sketch, "E356", {"start": v(12.17, 24.1) * mm, "end": v(12.3, 22.38) * mm});
            skLineSegment(sketch, "E357", {"start": v(12.3, 22.38) * mm, "end": v(12.2, 21.25) * mm});
            skLineSegment(sketch, "E358", {"start": v(12.2, 21.25) * mm, "end": v(12.04, 19.38) * mm});
            skLineSegment(sketch, "E359", {"start": v(12.04, 19.38) * mm, "end": v(12.22, 17.66) * mm});
            skLineSegment(sketch, "E360", {"start": v(12.22, 17.66) * mm, "end": v(12.64, 16.83) * mm});
            skLineSegment(sketch, "E361", {"start": v(12.64, 16.83) * mm, "end": v(13.44, 17.89) * mm});
            skLineSegment(sketch, "E362", {"start": v(13.44, 17.89) * mm, "end": v(14.35, 20.15) * mm});
            skLineSegment(sketch, "E363", {"start": v(14.35, 20.15) * mm, "end": v(14.73, 21.46) * mm});
            skLineSegment(sketch, "E364", {"start": v(14.73, 21.46) * mm, "end": v(14.77, 22.13) * mm});
            skLineSegment(sketch, "E365", {"start": v(14.77, 22.13) * mm, "end": v(14.24, 21.5) * mm});
            skLineSegment(sketch, "E366", {"start": v(14.24, 21.5) * mm, "end": v(13.84, 19.96) * mm});
            skLineSegment(sketch, "E367", {"start": v(13.84, 19.96) * mm, "end": v(13.23, 18.96) * mm});
            skLineSegment(sketch, "E368", {"start": v(13.23, 18.96) * mm, "end": v(12.76, 18.76) * mm});
            skLineSegment(sketch, "E369", {"start": v(12.76, 18.76) * mm, "end": v(12.34, 19.02) * mm});
            skLineSegment(sketch, "E370", {"start": v(12.34, 19.02) * mm, "end": v(12.69, 19.9) * mm});
            skLineSegment(sketch, "E371", {"start": v(12.69, 19.9) * mm, "end": v(13.08, 21.57) * mm});
            skLineSegment(sketch, "E372", {"start": v(13.08, 21.57) * mm, "end": v(13.1, 22.67) * mm});
            skLineSegment(sketch, "E373", {"start": v(13.1, 22.67) * mm, "end": v(12.17, 24.1) * mm});
            skLineSegment(sketch, "E374", {"start": v(13.58, 24.26) * mm, "end": v(14.28, 23.06) * mm});
            skLineSegment(sketch, "E375", {"start": v(14.28, 23.06) * mm, "end": v(14.6, 23.1) * mm});
            skLineSegment(sketch, "E376", {"start": v(14.6, 23.1) * mm, "end": v(13.58, 24.26) * mm});
            skLineSegment(sketch, "E377", {"start": v(10.23, 22.73) * mm, "end": v(10.21, 24.14) * mm});
            skLineSegment(sketch, "E378", {"start": v(10.21, 24.14) * mm, "end": v(10.44, 23.31) * mm});
            skLineSegment(sketch, "E379", {"start": v(10.44, 23.31) * mm, "end": v(10.38, 22.7) * mm});
            skLineSegment(sketch, "E380", {"start": v(10.38, 22.7) * mm, "end": v(10.23, 22.73) * mm});
            skSolve(sketch);
        }
        {
            var Q0;
            {var subQ4=sQuery(id+"F4.wireOp",EDGE,"E69");Q0=makeQuery(id+"F4.imprint","IMPRINT",FACE,{"disambiguationData":[TD([[makeQuery(id+"F4.imprint","IMPRINT",EDGE,{"derivedFrom":subQ4}),-1.0]])]});}
            var Q1;
            Q1=makeQuery(id+"F4.imprint","IMPRINT",FACE,{"disambiguationData":[TD([[makeQuery(id+"F4.imprint","IMPRINT",EDGE,{"derivedFrom":sQuery(id+"F4.wireOp",EDGE,"E338")}),-1.0]])]});
            var Q2;
            Q2=makeQuery(id+"F4.imprint","IMPRINT",FACE,{"disambiguationData":[TD([[makeQuery(id+"F4.imprint","IMPRINT",EDGE,{"derivedFrom":sQuery(id+"F4.wireOp",EDGE,"E356")}),1.0]])]});
            var Q3;
            Q3=makeQuery(id+"F4.imprint","IMPRINT",FACE,{"disambiguationData":[TD([[makeQuery(id+"F4.imprint","IMPRINT",EDGE,{"derivedFrom":sQuery(id+"F4.wireOp",EDGE,"E377")}),-1.0]])]});
            var Q4;
            Q4=makeQuery(id+"F4.imprint","IMPRINT",FACE,{"disambiguationData":[TD([[makeQuery(id+"F4.imprint","IMPRINT",EDGE,{"derivedFrom":sQuery(id+"F4.wireOp",EDGE,"E374")}),1.0]])]});
            var Q5;
            Q5=makeQuery(id+"F4.imprint","IMPRINT",FACE,{"disambiguationData":[TD([[makeQuery(id+"F4.imprint","IMPRINT",EDGE,{"derivedFrom":sQuery(id+"F4.wireOp",EDGE,"E289")}),1.0]])]});
            var Q6;
            Q6=makeQuery(id+"F4.imprint","IMPRINT",FACE,{"disambiguationData":[TD([[makeQuery(id+"F4.imprint","IMPRINT",EDGE,{"derivedFrom":sQuery(id+"F4.wireOp",EDGE,"E259")}),1.0]])]});
            extrude(context, id + "F5", {"entities" : qUnion([Q0, Q1, Q2, Q3, Q4, Q5, Q6]), "operationType" : NewBodyOperationType.REMOVE, "oppositeDirection" : true, "depth" : 1 * mm, "offsetDistance" : 25 * mm});
        }
        {
            var Q0;
            {var subQ120=sQuery(id+"F1.wireOp",EDGE,"E68");var subQ122=sQuery(id+"F1.wireOp",EDGE,"E66");var subQ124=sQuery(id+"F1.wireOp",EDGE,"E65");var subQ126=sQuery(id+"F1.wireOp",EDGE,"E64");var subQ128=sQuery(id+"F1.wireOp",EDGE,"E63");var subQ132=sQuery(id+"F1.wireOp",EDGE,"E62");var subQ135=sQuery(id+"F1.wireOp",EDGE,"E61");var subQ138=sQuery(id+"F1.wireOp",EDGE,"E60");var subQ142=sQuery(id+"F1.wireOp",EDGE,"E59");var subQ145=sQuery(id+"F1.wireOp",EDGE,"E58");var subQ148=sQuery(id+"F1.wireOp",EDGE,"E57");var subQ151=sQuery(id+"F1.wireOp",EDGE,"E56");var subQ154=sQuery(id+"F1.wireOp",EDGE,"E55");var subQ157=sQuery(id+"F1.wireOp",EDGE,"E54");var subQ160=sQuery(id+"F1.wireOp",EDGE,"E53");var subQ163=sQuery(id+"F1.wireOp",EDGE,"E52");var subQ166=sQuery(id+"F1.wireOp",EDGE,"E51");var subQ169=sQuery(id+"F1.wireOp",EDGE,"E50");var subQ172=sQuery(id+"F1.wireOp",EDGE,"E49");var subQ175=sQuery(id+"F1.wireOp",EDGE,"E48");var subQ178=sQuery(id+"F1.wireOp",EDGE,"E47");var subQ181=sQuery(id+"F1.wireOp",EDGE,"E46");var subQ184=sQuery(id+"F1.wireOp",EDGE,"E45");var subQ187=sQuery(id+"F1.wireOp",EDGE,"E44");var subQ190=sQuery(id+"F1.wireOp",EDGE,"E43");var subQ191=sQuery(id+"F0.wireOp",EDGE,"E1");var subQ195=sQuery(id+"F1.wireOp",EDGE,"E42");var subQ198=sQuery(id+"F1.wireOp",EDGE,"E41");var subQ199=sQuery(id+"F1.wireOp",EDGE,"E40");var subQ200=sQuery(id+"F0.wireOp",EDGE,"E0");var subQ201=makeQuery(id+"F2.opExtrude","SWEPT_FACE",FACE,{"disambiguationData":[OSD([subQ200])]});var subQ204=sQuery(id+"F1.wireOp",EDGE,"E39");var subQ207=sQuery(id+"F1.wireOp",EDGE,"E38");var subQ210=sQuery(id+"F1.wireOp",EDGE,"E37");var subQ213=sQuery(id+"F1.wireOp",EDGE,"E36");var subQ216=sQuery(id+"F1.wireOp",EDGE,"E35");var subQ219=sQuery(id+"F1.wireOp",EDGE,"E34");var subQ222=sQuery(id+"F1.wireOp",EDGE,"E33");var subQ225=sQuery(id+"F1.wireOp",EDGE,"E32");var subQ228=sQuery(id+"F1.wireOp",EDGE,"E31");var subQ231=sQuery(id+"F1.wireOp",EDGE,"E30");var subQ234=sQuery(id+"F1.wireOp",EDGE,"E29");var subQ237=sQuery(id+"F1.wireOp",EDGE,"E28");var subQ240=sQuery(id+"F1.wireOp",EDGE,"E27");var subQ243=sQuery(id+"F1.wireOp",EDGE,"E26");var subQ246=sQuery(id+"F1.wireOp",EDGE,"E25");var subQ249=sQuery(id+"F1.wireOp",EDGE,"E24");var subQ252=sQuery(id+"F1.wireOp",EDGE,"E23");var subQ255=sQuery(id+"F1.wireOp",EDGE,"E22");var subQ258=sQuery(id+"F1.wireOp",EDGE,"E21");var subQ261=sQuery(id+"F1.wireOp",EDGE,"E20");var subQ264=sQuery(id+"F1.wireOp",EDGE,"E19");var subQ267=sQuery(id+"F1.wireOp",EDGE,"E18");var subQ270=sQuery(id+"F1.wireOp",EDGE,"E17");var subQ273=sQuery(id+"F1.wireOp",EDGE,"E16");var subQ276=sQuery(id+"F1.wireOp",EDGE,"E15");var subQ279=sQuery(id+"F1.wireOp",EDGE,"E14");var subQ282=sQuery(id+"F1.wireOp",EDGE,"E13");var subQ285=sQuery(id+"F1.wireOp",EDGE,"E12");var subQ288=sQuery(id+"F1.wireOp",EDGE,"E11");var subQ291=sQuery(id+"F1.wireOp",EDGE,"E10");var subQ294=sQuery(id+"F1.wireOp",EDGE,"E9");var subQ297=sQuery(id+"F1.wireOp",EDGE,"E7");var subQ1208=sQuery(id+"F1.wireOp",EDGE,"E67");var subQ1209=sQuery(id+"F1.wireOp",EDGE,"E8");var subQ1210=sQuery(id+"F1.wireOp",EDGE,"E6.0");Q0=makeQuery(id+"FciJOSwSTCKuNuW_1.2.F5.boolean.opBoolean","SPLIT",FACE,{"disambiguationData":[TD([subQ201])],"derivedFrom":makeQuery(id+"FciJOSwSTCKuNuW_1.2.F3.boolean.opBoolean","MERGE",FACE,{"derivedFrom":[makeQuery(id+"FciJOSwSTCKuNuW_1.1.F5.boolean.opBoolean","SPLIT",FACE,{"disambiguationData":[TD([subQ201])],"derivedFrom":makeQuery(id+"FciJOSwSTCKuNuW_1.1.F3.boolean.opBoolean","MERGE",FACE,{"derivedFrom":[makeQuery(id+"F5.boolean.opBoolean","SPLIT",FACE,{"disambiguationData":[TD([subQ201])],"derivedFrom":makeQuery(id+"F3.boolean.opBoolean","MERGE",FACE,{"derivedFrom":[makeQuery(id+"F2.opExtrude","CAP_FACE",FACE,{"disambiguationData":[OSD([subQ200,subQ191])],"isStart":false}),makeQuery(id+"F3.opExtrude","CAP_FACE",FACE,{"disambiguationData":[OSD([subQ1210,subQ297,subQ1209,subQ294,subQ291,subQ288,subQ285,subQ282,subQ279,subQ276,subQ273,subQ270,subQ267,subQ264,subQ261,subQ258,subQ255,subQ252,subQ249,subQ246,subQ243,subQ240,subQ237,subQ234,subQ231,subQ228,subQ225,subQ222,subQ219,subQ216,subQ213,subQ210,subQ207,subQ204,subQ199,subQ198,subQ195,subQ190,subQ187,subQ184,subQ181,subQ178,subQ175,subQ172,subQ169,subQ166,subQ163,subQ160,subQ157,subQ154,subQ151,subQ148,subQ145,subQ142,subQ138,subQ135,subQ132,subQ128,subQ126,subQ124,subQ122,subQ1208,subQ120])],"isStart":false})]})}),makeQuery(id+"FciJOSwSTCKuNuW_1.1.F3.opExtrude","CAP_FACE",FACE,{"disambiguationData":[OSD([subQ1210,subQ297,subQ1209,subQ294,subQ291,subQ288,subQ285,subQ282,subQ279,subQ276,subQ273,subQ270,subQ267,subQ264,subQ261,subQ258,subQ255,subQ252,subQ249,subQ246,subQ243,subQ240,subQ237,subQ234,subQ231,subQ228,subQ225,subQ222,subQ219,subQ216,subQ213,subQ210,subQ207,subQ204,subQ199,subQ198,subQ195,subQ190,subQ187,subQ184,subQ181,subQ178,subQ175,subQ172,subQ169,subQ166,subQ163,subQ160,subQ157,subQ154,subQ151,subQ148,subQ145,subQ142,subQ138,subQ135,subQ132,subQ128,subQ126,subQ124,subQ122,subQ1208,subQ120])],"isStart":false})]})}),makeQuery(id+"FciJOSwSTCKuNuW_1.2.F3.opExtrude","CAP_FACE",FACE,{"disambiguationData":[OSD([subQ1210,subQ297,subQ1209,subQ294,subQ291,subQ288,subQ285,subQ282,subQ279,subQ276,subQ273,subQ270,subQ267,subQ264,subQ261,subQ258,subQ255,subQ252,subQ249,subQ246,subQ243,subQ240,subQ237,subQ234,subQ231,subQ228,subQ225,subQ222,subQ219,subQ216,subQ213,subQ210,subQ207,subQ204,subQ199,subQ198,subQ195,subQ190,subQ187,subQ184,subQ181,subQ178,subQ175,subQ172,subQ169,subQ166,subQ163,subQ160,subQ157,subQ154,subQ151,subQ148,subQ145,subQ142,subQ138,subQ135,subQ132,subQ128,subQ126,subQ124,subQ122,subQ1208,subQ120])],"isStart":false})]})});}
            var sketch = newSketch(context, id + "F6", { "sketchPlane" : qUnion([Q0])});
            skCircle(sketch, "E381", {"center": v(0.17, -13.44) * mm, "radius": 0.26 * mm});
            skCircle(sketch, "E382", {"center": v(-11.76, 6.57) * mm, "radius": 0.2 * mm});
            skCircle(sketch, "E383", {"center": v(11.56, 6.91) * mm, "radius": 0.2 * mm});
            skSolve(sketch);
        }
        {
            var Q0;
            Q0=qSketchRegion(id+"F6",true);
            extrude(context, id + "F7", {"entities" : qUnion([Q0]), "operationType" : NewBodyOperationType.ADD, "oppositeDirection" : true, "depth" : 7 * mm, "offsetDistance" : 25 * mm});
        }
        {
            var Q0;
            {var subQ120=sQuery(id+"F1.wireOp",EDGE,"E68");var subQ122=sQuery(id+"F1.wireOp",EDGE,"E66");var subQ124=sQuery(id+"F1.wireOp",EDGE,"E65");var subQ126=sQuery(id+"F1.wireOp",EDGE,"E64");var subQ128=sQuery(id+"F1.wireOp",EDGE,"E63");var subQ132=sQuery(id+"F1.wireOp",EDGE,"E62");var subQ135=sQuery(id+"F1.wireOp",EDGE,"E61");var subQ138=sQuery(id+"F1.wireOp",EDGE,"E60");var subQ142=sQuery(id+"F1.wireOp",EDGE,"E59");var subQ145=sQuery(id+"F1.wireOp",EDGE,"E58");var subQ148=sQuery(id+"F1.wireOp",EDGE,"E57");var subQ151=sQuery(id+"F1.wireOp",EDGE,"E56");var subQ154=sQuery(id+"F1.wireOp",EDGE,"E55");var subQ157=sQuery(id+"F1.wireOp",EDGE,"E54");var subQ160=sQuery(id+"F1.wireOp",EDGE,"E53");var subQ163=sQuery(id+"F1.wireOp",EDGE,"E52");var subQ166=sQuery(id+"F1.wireOp",EDGE,"E51");var subQ169=sQuery(id+"F1.wireOp",EDGE,"E50");var subQ172=sQuery(id+"F1.wireOp",EDGE,"E49");var subQ175=sQuery(id+"F1.wireOp",EDGE,"E48");var subQ178=sQuery(id+"F1.wireOp",EDGE,"E47");var subQ181=sQuery(id+"F1.wireOp",EDGE,"E46");var subQ184=sQuery(id+"F1.wireOp",EDGE,"E45");var subQ187=sQuery(id+"F1.wireOp",EDGE,"E44");var subQ190=sQuery(id+"F1.wireOp",EDGE,"E43");var subQ191=sQuery(id+"F0.wireOp",EDGE,"E1");var subQ195=sQuery(id+"F1.wireOp",EDGE,"E42");var subQ198=sQuery(id+"F1.wireOp",EDGE,"E41");var subQ199=sQuery(id+"F1.wireOp",EDGE,"E40");var subQ200=sQuery(id+"F0.wireOp",EDGE,"E0");var subQ201=makeQuery(id+"F2.opExtrude","SWEPT_FACE",FACE,{"disambiguationData":[OSD([subQ200])]});var subQ204=sQuery(id+"F1.wireOp",EDGE,"E39");var subQ207=sQuery(id+"F1.wireOp",EDGE,"E38");var subQ210=sQuery(id+"F1.wireOp",EDGE,"E37");var subQ213=sQuery(id+"F1.wireOp",EDGE,"E36");var subQ216=sQuery(id+"F1.wireOp",EDGE,"E35");var subQ219=sQuery(id+"F1.wireOp",EDGE,"E34");var subQ222=sQuery(id+"F1.wireOp",EDGE,"E33");var subQ225=sQuery(id+"F1.wireOp",EDGE,"E32");var subQ228=sQuery(id+"F1.wireOp",EDGE,"E31");var subQ231=sQuery(id+"F1.wireOp",EDGE,"E30");var subQ234=sQuery(id+"F1.wireOp",EDGE,"E29");var subQ237=sQuery(id+"F1.wireOp",EDGE,"E28");var subQ240=sQuery(id+"F1.wireOp",EDGE,"E27");var subQ243=sQuery(id+"F1.wireOp",EDGE,"E26");var subQ246=sQuery(id+"F1.wireOp",EDGE,"E25");var subQ249=sQuery(id+"F1.wireOp",EDGE,"E24");var subQ252=sQuery(id+"F1.wireOp",EDGE,"E23");var subQ255=sQuery(id+"F1.wireOp",EDGE,"E22");var subQ258=sQuery(id+"F1.wireOp",EDGE,"E21");var subQ261=sQuery(id+"F1.wireOp",EDGE,"E20");var subQ264=sQuery(id+"F1.wireOp",EDGE,"E19");var subQ267=sQuery(id+"F1.wireOp",EDGE,"E18");var subQ270=sQuery(id+"F1.wireOp",EDGE,"E17");var subQ273=sQuery(id+"F1.wireOp",EDGE,"E16");var subQ276=sQuery(id+"F1.wireOp",EDGE,"E15");var subQ279=sQuery(id+"F1.wireOp",EDGE,"E14");var subQ282=sQuery(id+"F1.wireOp",EDGE,"E13");var subQ285=sQuery(id+"F1.wireOp",EDGE,"E12");var subQ288=sQuery(id+"F1.wireOp",EDGE,"E11");var subQ291=sQuery(id+"F1.wireOp",EDGE,"E10");var subQ294=sQuery(id+"F1.wireOp",EDGE,"E9");var subQ297=sQuery(id+"F1.wireOp",EDGE,"E7");var subQ1208=sQuery(id+"F1.wireOp",EDGE,"E67");var subQ1209=sQuery(id+"F1.wireOp",EDGE,"E8");var subQ1210=sQuery(id+"F1.wireOp",EDGE,"E6.0");Q0=makeQuery(id+"F7.boolean.opBoolean","MERGE",FACE,{"derivedFrom":[makeQuery(id+"FciJOSwSTCKuNuW_1.2.F5.boolean.opBoolean","SPLIT",FACE,{"disambiguationData":[TD([subQ201])],"derivedFrom":makeQuery(id+"FciJOSwSTCKuNuW_1.2.F3.boolean.opBoolean","MERGE",FACE,{"derivedFrom":[makeQuery(id+"FciJOSwSTCKuNuW_1.1.F5.boolean.opBoolean","SPLIT",FACE,{"disambiguationData":[TD([subQ201])],"derivedFrom":makeQuery(id+"FciJOSwSTCKuNuW_1.1.F3.boolean.opBoolean","MERGE",FACE,{"derivedFrom":[makeQuery(id+"F5.boolean.opBoolean","SPLIT",FACE,{"disambiguationData":[TD([subQ201])],"derivedFrom":makeQuery(id+"F3.boolean.opBoolean","MERGE",FACE,{"derivedFrom":[makeQuery(id+"F2.opExtrude","CAP_FACE",FACE,{"disambiguationData":[OSD([subQ200,subQ191])],"isStart":false}),makeQuery(id+"F3.opExtrude","CAP_FACE",FACE,{"disambiguationData":[OSD([subQ1210,subQ297,subQ1209,subQ294,subQ291,subQ288,subQ285,subQ282,subQ279,subQ276,subQ273,subQ270,subQ267,subQ264,subQ261,subQ258,subQ255,subQ252,subQ249,subQ246,subQ243,subQ240,subQ237,subQ234,subQ231,subQ228,subQ225,subQ222,subQ219,subQ216,subQ213,subQ210,subQ207,subQ204,subQ199,subQ198,subQ195,subQ190,subQ187,subQ184,subQ181,subQ178,subQ175,subQ172,subQ169,subQ166,subQ163,subQ160,subQ157,subQ154,subQ151,subQ148,subQ145,subQ142,subQ138,subQ135,subQ132,subQ128,subQ126,subQ124,subQ122,subQ1208,subQ120])],"isStart":false})]})}),makeQuery(id+"FciJOSwSTCKuNuW_1.1.F3.opExtrude","CAP_FACE",FACE,{"disambiguationData":[OSD([subQ1210,subQ297,subQ1209,subQ294,subQ291,subQ288,subQ285,subQ282,subQ279,subQ276,subQ273,subQ270,subQ267,subQ264,subQ261,subQ258,subQ255,subQ252,subQ249,subQ246,subQ243,subQ240,subQ237,subQ234,subQ231,subQ228,subQ225,subQ222,subQ219,subQ216,subQ213,subQ210,subQ207,subQ204,subQ199,subQ198,subQ195,subQ190,subQ187,subQ184,subQ181,subQ178,subQ175,subQ172,subQ169,subQ166,subQ163,subQ160,subQ157,subQ154,subQ151,subQ148,subQ145,subQ142,subQ138,subQ135,subQ132,subQ128,subQ126,subQ124,subQ122,subQ1208,subQ120])],"isStart":false})]})}),makeQuery(id+"FciJOSwSTCKuNuW_1.2.F3.opExtrude","CAP_FACE",FACE,{"disambiguationData":[OSD([subQ1210,subQ297,subQ1209,subQ294,subQ291,subQ288,subQ285,subQ282,subQ279,subQ276,subQ273,subQ270,subQ267,subQ264,subQ261,subQ258,subQ255,subQ252,subQ249,subQ246,subQ243,subQ240,subQ237,subQ234,subQ231,subQ228,subQ225,subQ222,subQ219,subQ216,subQ213,subQ210,subQ207,subQ204,subQ199,subQ198,subQ195,subQ190,subQ187,subQ184,subQ181,subQ178,subQ175,subQ172,subQ169,subQ166,subQ163,subQ160,subQ157,subQ154,subQ151,subQ148,subQ145,subQ142,subQ138,subQ135,subQ132,subQ128,subQ126,subQ124,subQ122,subQ1208,subQ120])],"isStart":false})]})}),makeQuery(id+"F7.opExtrude","CAP_FACE",FACE,{"disambiguationData":[OSD([sQuery(id+"F6.wireOp",EDGE,"E381")])],"isStart":true}),makeQuery(id+"F7.opExtrude","CAP_FACE",FACE,{"disambiguationData":[OSD([sQuery(id+"F6.wireOp",EDGE,"E382")])],"isStart":true}),makeQuery(id+"F7.opExtrude","CAP_FACE",FACE,{"disambiguationData":[OSD([sQuery(id+"F6.wireOp",EDGE,"E383")])],"isStart":true})]});}
            var sketch = newSketch(context, id + "F8", { "sketchPlane" : qUnion([Q0])});
            skCircle(sketch, "E384", {"center": v(-30.86, 14.49) * mm, "radius": 11 * mm});
            skCircle(sketch, "E385", {"center": v(-30.86, 14.49) * mm, "radius": 13.4 * mm});
            skLineSegment(sketch, "E386", {"start": v(-30.86, 14.49) * mm, "end": v(0, 0) * mm, "construction": true});
            skLineSegment(sketch, "E387", {"start": v(-30.86, 14.49) * mm, "end": v(-32, 27.84) * mm});
            skLineSegment(sketch, "E388", {"start": v(-30.86, 14.49) * mm, "end": v(-41.86, 6.83) * mm});
            skSolve(sketch);
        }
        {
            var Q0;
            {var subQ11=makeQuery(id+"F3.opExtrude","CAP_EDGE",EDGE,{"disambiguationData":[OSD([sQuery(id+"F1.wireOp",EDGE,"E12")])],"isStart":false});Q0=makeQuery(id+"F8.imprint","IMPRINT",FACE,{"disambiguationData":[TD([[makeQuery(id+"F8.imprint","IMPRINT",EDGE,{"derivedFrom":subQ11}),1.0]])]});}
            var Q1;
            {var subQ1=makeQuery(id+"F3.opExtrude","CAP_EDGE",EDGE,{"disambiguationData":[OSD([sQuery(id+"F1.wireOp",EDGE,"E10")])],"isStart":false});Q1=makeQuery(id+"F8.imprint","IMPRINT",FACE,{"disambiguationData":[TD([[makeQuery(id+"F8.imprint","IMPRINT",EDGE,{"derivedFrom":subQ1}),1.0]])]});}
            var Q2;
            {var subQ0=sQuery(id+"F8.wireOp",EDGE,"E387");var subQ1=sQuery(id+"F8.wireOp",EDGE,"E384");var subQ2=makeQuery(id+"F8.imprint","INTERSECT",VERTEX,{"derivedFrom":[subQ1,subQ0]});Q2=makeQuery(id+"F8.imprint","IMPRINT",FACE,{"disambiguationData":[TD([[makeQuery(id+"F8.imprint","IMPRINT",EDGE,{"disambiguationData":[TD([[subQ2,-1.0]])],"derivedFrom":subQ1}),-1.0]])]});}
            extrude(context, id + "F9", {"entities" : qUnion([Q0, Q1, Q2]), "operationType" : NewBodyOperationType.ADD, "oppositeDirection" : true, "depth" : 7 * mm, "offsetDistance" : 25 * mm});
        }
    });
